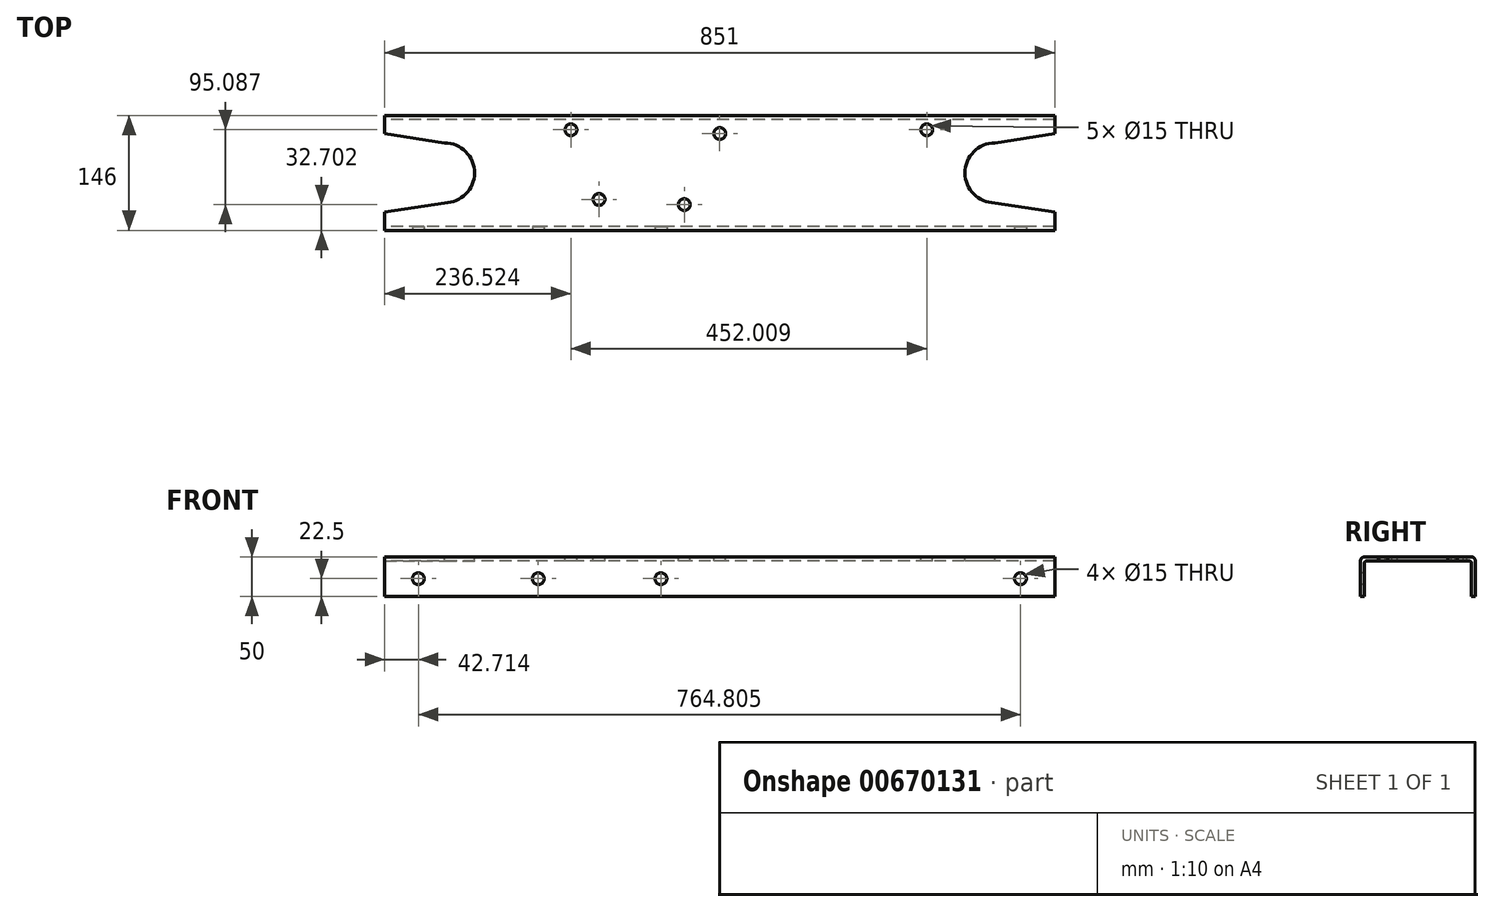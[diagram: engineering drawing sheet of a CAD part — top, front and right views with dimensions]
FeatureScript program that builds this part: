
annotation { "Feature Type Name" : "Feature", "Feature Type Description" : "" }
export const myFeature = defineFeature(function(context is Context, id is Id, definition is map)
    precondition{}
    {
        {
            var Q0;
            Q0=qCreatedBy(makeId("Right.planeOp"),FACE);
            var sketch = newSketch(context, id + "F0", { "sketchPlane" : qUnion([Q0])});
            skLineSegment(sketch, "E0", {"start": v(0, 0) * mm, "end": v(0, -15.8) * mm});
            skPoint(sketch, "E1.orphan", {"position": v(0, 5) * mm});
            skLineSegment(sketch, "E2", {"start": v(0, 0) * mm, "end": v(-68, 0) * mm});
            skLineSegment(sketch, "E3", {"start": v(-73, -5) * mm, "end": v(-73, -50) * mm});
            skLineSegment(sketch, "E4", {"start": v(-73, -50) * mm, "end": v(-68, -50) * mm});
            skLineSegment(sketch, "E5", {"start": v(-68, -50) * mm, "end": v(-68, -8) * mm});
            skLineSegment(sketch, "E6", {"start": v(-65, -5) * mm, "end": v(0, -5) * mm});
            skLineSegment(sketch, "E7.MirrorCS", {"start": v(65, -5) * mm, "end": v(0, -5) * mm});
            skLineSegment(sketch, "E8.MirrorCS", {"start": v(0, 0) * mm, "end": v(68, 0) * mm});
            skLineSegment(sketch, "E9.MirrorCS", {"start": v(73, -5) * mm, "end": v(73, -50) * mm});
            skLineSegment(sketch, "E10.MirrorCS", {"start": v(68, -50) * mm, "end": v(68, -8) * mm});
            skLineSegment(sketch, "E11.MirrorCS", {"start": v(73, -50) * mm, "end": v(68, -50) * mm});
            skPoint(sketch, "E12.visualSharp", {"position": v(-73, 0) * mm});
            skArc(sketch, "E12.filletArc", {"start": v(-68, 0) * mm, "mid": v(-71.54, -1.46) * mm, "end": v(-73, -5) * mm});
            skArc(sketch, "E13.filletArc", {"start": v(-65, -5) * mm, "mid": v(-67.12, -5.88) * mm, "end": v(-68, -8) * mm});
            skArc(sketch, "E14.MirrorCS", {"start": v(65, -5) * mm, "mid": v(67.12, -5.88) * mm, "end": v(68, -8) * mm});
            skArc(sketch, "E15.MirrorCS", {"start": v(68, 0) * mm, "mid": v(71.54, -1.46) * mm, "end": v(73, -5) * mm});
            skPoint(sketch, "E16.orphan", {"position": v(73, 0) * mm});
            skSolve(sketch);
        }
        {
            var Q0;
            Q0 = qSketchRegion(id + "F0", true);
            extrude(context, id + "F1", {"entities" : qUnion([Q0]), "endBound" : BoundingType.SYMMETRIC, "depth" : 851 * mm, "offsetDistance" : 25 * mm});
        }
        {
            var Q0;
            Q0=makeQuery(id+"F1.opExtrude","SWEPT_FACE",FACE,{"disambiguationData":[OSD([sQuery(id+"F0.wireOp",EDGE,"E2"),sQuery(id+"F0.wireOp",EDGE,"E8.MirrorCS")])]});
            var sketch = newSketch(context, id + "F2", { "sketchPlane" : qUnion([Q0])});
            skLineSegment(sketch, "E17", {"start": v(-425.5, 68) * mm, "end": v(-425.5, 0) * mm});
            skLineSegment(sketch, "E18", {"start": v(-425.5, 0) * mm, "end": v(-425.5, 50) * mm});
            skLineSegment(sketch, "E19", {"start": v(-425.5, 50) * mm, "end": v(-425.5, -50) * mm});
            skArc(sketch, "E20", {"start": v(-349.5, -38) * mm, "mid": v(-311.5, 0) * mm, "end": v(-349.5, 38) * mm});
            skLineSegment(sketch, "E21", {"start": v(-425.5, 50) * mm, "end": v(-349.5, 38) * mm});
            skLineSegment(sketch, "E22", {"start": v(-349.5, -38) * mm, "end": v(-425.5, -50) * mm});
            skLineSegment(sketch, "E23", {"start": v(0, 0) * mm, "end": v(0, 93.22) * mm});
            skPoint(sketch, "E23.endSnap0", {"position": v(0, 68) * mm});
            skArc(sketch, "E24.MirrorCS", {"start": v(349.5, -38) * mm, "mid": v(311.5, 0) * mm, "end": v(349.5, 38) * mm});
            skLineSegment(sketch, "E25.MirrorCS", {"start": v(425.5, 50) * mm, "end": v(349.5, 38) * mm});
            skLineSegment(sketch, "E26.MirrorCS", {"start": v(349.5, -38) * mm, "end": v(425.5, -50) * mm});
            skLineSegment(sketch, "E27.MirrorCS", {"start": v(425.5, 50) * mm, "end": v(425.5, -50) * mm});
            skCircle(sketch, "E28", {"center": v(-188.98, 54.79) * mm, "radius": 7.5 * mm});
            skCircle(sketch, "E29", {"center": v(0, 50) * mm, "radius": 7.5 * mm});
            skCircle(sketch, "E30", {"center": v(263.03, 54.79) * mm, "radius": 7.5 * mm});
            skCircle(sketch, "E31", {"center": v(-153.3, -33.8) * mm, "radius": 7.5 * mm});
            skCircle(sketch, "E32", {"center": v(-45.04, -40.3) * mm, "radius": 7.5 * mm});
            skSolve(sketch);
        }
        {
            var Q0;
            Q0 = qSketchRegion(id + "F2", true);
            extrude(context, id + "F3", {"entities" : qUnion([Q0]), "operationType" : NewBodyOperationType.REMOVE, "oppositeDirection" : true, "depth" : 81 * mm, "offsetDistance" : 25 * mm});
        }
        {
            var Q0;
            Q0=makeQuery(id+"F1.opExtrude","SWEPT_FACE",FACE,{"disambiguationData":[OSD([sQuery(id+"F0.wireOp",EDGE,"E3")])]});
            var sketch = newSketch(context, id + "F4", { "sketchPlane" : qUnion([Q0])});
            skCircle(sketch, "E33.0", {"center": v(-382.79, -27.5) * mm, "radius": 7.5 * mm});
            skCircle(sketch, "E34.0", {"center": v(382.02, -27.5) * mm, "radius": 7.5 * mm});
            skCircle(sketch, "E35", {"center": v(-230.55, -27.5) * mm, "radius": 7.5 * mm});
            skCircle(sketch, "E36", {"center": v(-74.7, -27.5) * mm, "radius": 7.5 * mm});
            skSolve(sketch);
        }
        {
            var Q0;
            Q0=makeQuery(id+"F4.imprint","IMPRINT",FACE,{"disambiguationData":[TD([[makeQuery(id+"F4.imprint","IMPRINT",EDGE,{"derivedFrom":sQuery(id+"F4.wireOp",EDGE,"E33.0")}),1.0]])]});
            var Q1;
            Q1=makeQuery(id+"F4.imprint","IMPRINT",FACE,{"disambiguationData":[TD([[makeQuery(id+"F4.imprint","IMPRINT",EDGE,{"derivedFrom":sQuery(id+"F4.wireOp",EDGE,"48f73899-b4e1-416e-bab3-4c8b3fd10c0e.0")}),1.0]])]});
            var Q2;
            Q2=makeQuery(id+"F4.imprint","IMPRINT",FACE,{"disambiguationData":[TD([[makeQuery(id+"F4.imprint","IMPRINT",EDGE,{"derivedFrom":sQuery(id+"F4.wireOp",EDGE,"07643aa1-5eab-4856-8365-762c126ab8f7.0")}),1.0]])]});
            var Q3;
            Q3=makeQuery(id+"F4.imprint","IMPRINT",FACE,{"disambiguationData":[TD([[makeQuery(id+"F4.imprint","IMPRINT",EDGE,{"derivedFrom":sQuery(id+"F4.wireOp",EDGE,"E34.0")}),1.0]])]});
            var Q4;
            Q4=makeQuery(id+"F4.imprint","IMPRINT",FACE,{"disambiguationData":[TD([[makeQuery(id+"F4.imprint","IMPRINT",EDGE,{"derivedFrom":sQuery(id+"F4.wireOp",EDGE,"E35")}),1.0]])]});
            var Q5;
            Q5=makeQuery(id+"F4.imprint","IMPRINT",FACE,{"disambiguationData":[TD([[makeQuery(id+"F4.imprint","IMPRINT",EDGE,{"derivedFrom":sQuery(id+"F4.wireOp",EDGE,"E36")}),1.0]])]});
            extrude(context, id + "F5", {"entities" : qUnion([Q0, Q1, Q2, Q3, Q4, Q5]), "operationType" : NewBodyOperationType.REMOVE, "oppositeDirection" : true, "depth" : 25 * mm, "offsetDistance" : 25 * mm});
        }
    });
